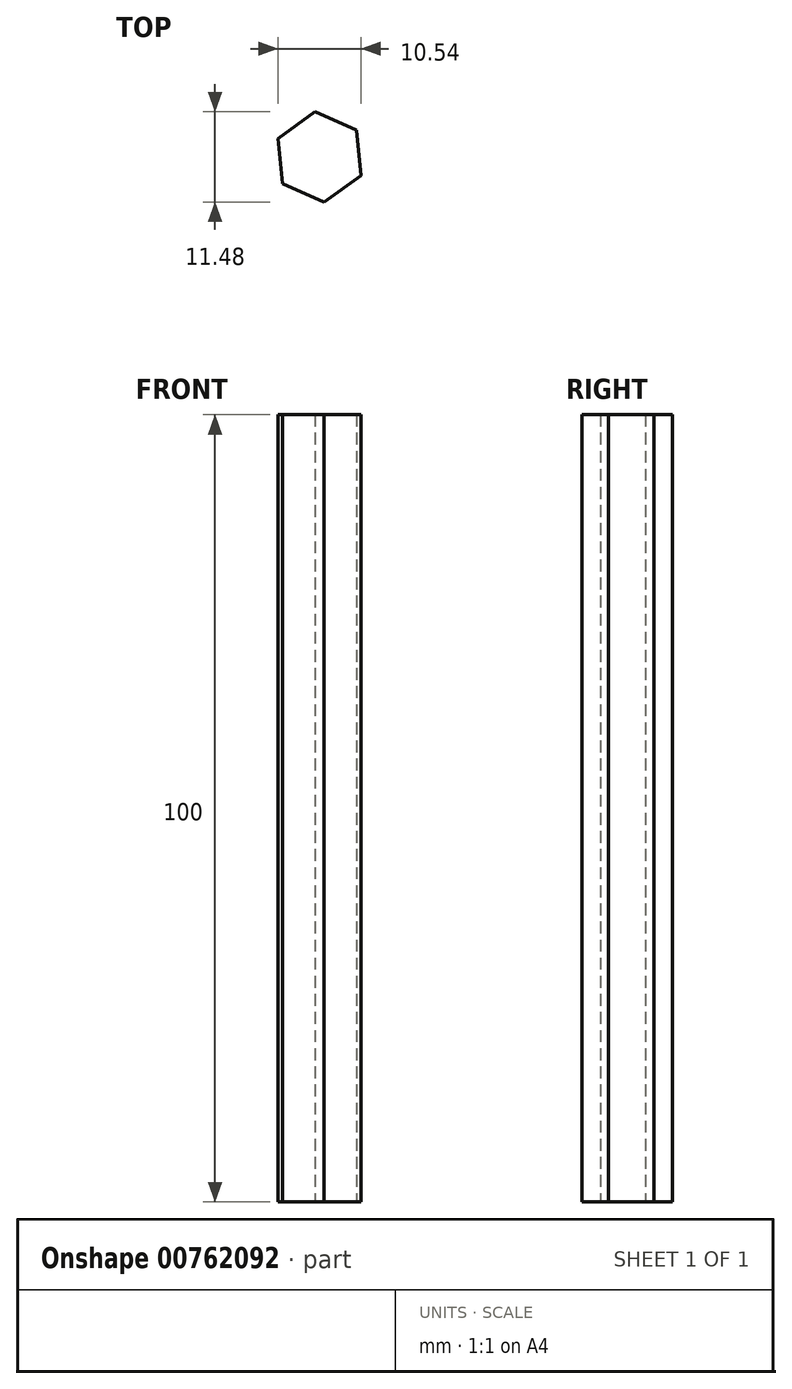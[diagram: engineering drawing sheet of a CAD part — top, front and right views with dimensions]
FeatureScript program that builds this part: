
annotation { "Feature Type Name" : "Feature", "Feature Type Description" : "" }
export const myFeature = defineFeature(function(context is Context, id is Id, definition is map)
    precondition{}
    {
        {
            var Q0;
            Q0=qCreatedBy(makeId("Top.planeOp"),FACE);
            var sketch = newSketch(context, id + "F0", { "sketchPlane" : qUnion([Q0])});
            skCircle(sketch, "E0.cCircle", {"center": v(0, 0) * mm, "radius": 5 * mm, "construction": true});
            skLineSegment(sketch, "E0.0", {"start": v(-5.27, 2.35) * mm, "end": v(-0.6, 5.74) * mm});
            skLineSegment(sketch, "E0.1", {"start": v(-0.6, 5.74) * mm, "end": v(4.67, 3.39) * mm});
            skLineSegment(sketch, "E0.2", {"start": v(4.67, 3.39) * mm, "end": v(5.27, -2.35) * mm});
            skLineSegment(sketch, "E0.3", {"start": v(5.27, -2.35) * mm, "end": v(0.6, -5.74) * mm});
            skLineSegment(sketch, "E0.4", {"start": v(0.6, -5.74) * mm, "end": v(-4.67, -3.39) * mm});
            skLineSegment(sketch, "E0.5", {"start": v(-4.67, -3.39) * mm, "end": v(-5.27, 2.35) * mm});
            skPoint(sketch, "E0.0.midPoint", {"position": v(-2.93, 4.05) * mm});
            skSolve(sketch);
        }
        {
            var Q0;
            Q0=makeQuery(id+"F0.imprint","IMPRINT",FACE,{"disambiguationData":[TD([[makeQuery(id+"F0.imprint","IMPRINT",EDGE,{"derivedFrom":sQuery(id+"F0.wireOp",EDGE,"E0.0")}),-1.0]])]});
            extrude(context, id + "F1", {"entities" : qUnion([Q0]), "depth" : 100 * mm, "offsetDistance" : 25 * mm});
        }
    });
